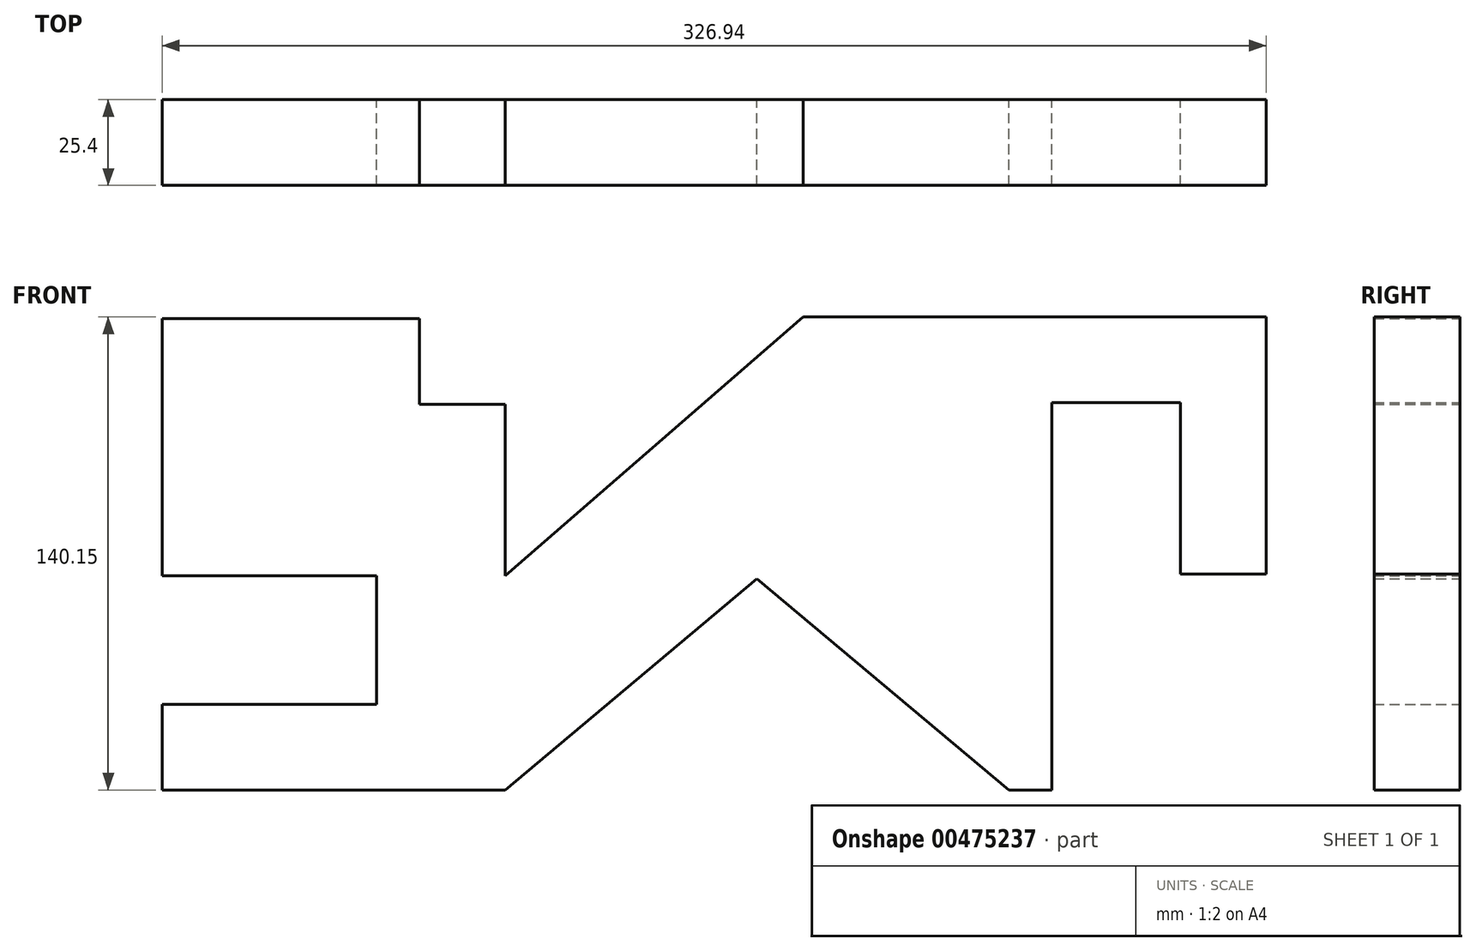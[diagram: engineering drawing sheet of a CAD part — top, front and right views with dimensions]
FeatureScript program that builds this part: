
annotation { "Feature Type Name" : "Feature", "Feature Type Description" : "" }
export const myFeature = defineFeature(function(context is Context, id is Id, definition is map)
    precondition{}
    {
        {
            var Q0;
            Q0=qCreatedBy(makeId("Front.planeOp"),FACE);
            var sketch = newSketch(context, id + "F0", { "sketchPlane" : qUnion([Q0])});
            skLineSegment(sketch, "E0", {"start": v(0, 0) * mm, "end": v(0, 76.2) * mm});
            skLineSegment(sketch, "E1", {"start": v(0, 76.2) * mm, "end": v(76.2, 76.2) * mm});
            skLineSegment(sketch, "E2", {"start": v(76.2, 76.2) * mm, "end": v(76.2, 50.8) * mm});
            skLineSegment(sketch, "E3", {"start": v(76.2, 50.8) * mm, "end": v(101.6, 50.8) * mm});
            skLineSegment(sketch, "E4", {"start": v(0, 0) * mm, "end": v(63.5, 0) * mm});
            skLineSegment(sketch, "E5", {"start": v(63.5, 0) * mm, "end": v(63.5, -38.1) * mm});
            skLineSegment(sketch, "E6", {"start": v(63.5, -38.1) * mm, "end": v(0, -38.1) * mm});
            skLineSegment(sketch, "E7", {"start": v(0, -38.1) * mm, "end": v(0, -63.5) * mm});
            skLineSegment(sketch, "E8", {"start": v(0, -63.5) * mm, "end": v(101.6, -63.5) * mm});
            skPoint(sketch, "E9.endSnap0", {"position": v(114.38, -63.5) * mm});
            skLineSegment(sketch, "E10", {"start": v(101.6, -63.5) * mm, "end": v(176.17, -0.93) * mm});
            skLineSegment(sketch, "E11", {"start": v(101.6, 50.8) * mm, "end": v(101.6, 0) * mm});
            skLineSegment(sketch, "E12", {"start": v(101.6, 0) * mm, "end": v(189.78, 76.65) * mm});
            skLineSegment(sketch, "E13", {"start": v(189.78, 76.65) * mm, "end": v(326.94, 76.65) * mm});
            skLineSegment(sketch, "E14", {"start": v(326.94, 76.65) * mm, "end": v(326.94, 0.45) * mm});
            skLineSegment(sketch, "E15", {"start": v(326.94, 0.45) * mm, "end": v(301.54, 0.45) * mm});
            skLineSegment(sketch, "E16", {"start": v(301.54, 0.45) * mm, "end": v(301.54, 51.25) * mm});
            skLineSegment(sketch, "E17", {"start": v(301.54, 51.25) * mm, "end": v(263.44, 51.25) * mm});
            skLineSegment(sketch, "E18", {"start": v(263.44, 51.25) * mm, "end": v(263.44, -63.5) * mm});
            skLineSegment(sketch, "E19", {"start": v(263.44, -63.5) * mm, "end": v(250.74, -63.5) * mm});
            skLineSegment(sketch, "E20", {"start": v(250.74, -63.5) * mm, "end": v(176.17, -0.93) * mm});
            skSolve(sketch);
        }
        {
            var Q0;
            Q0 = qSketchRegion(id + "F0", true);
            extrude(context, id + "F1", {"entities" : qUnion([Q0]), "depth" : 25.4 * mm});
        }
    });
